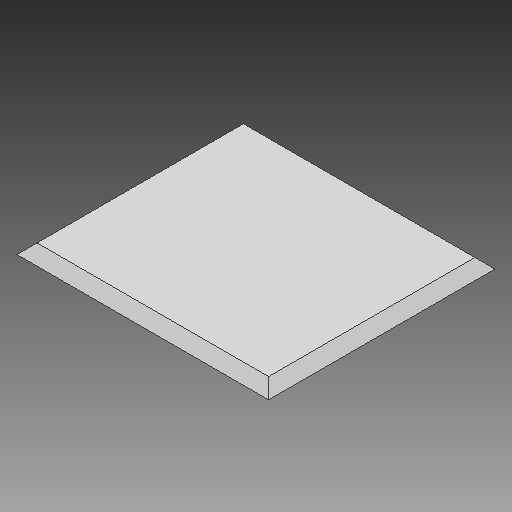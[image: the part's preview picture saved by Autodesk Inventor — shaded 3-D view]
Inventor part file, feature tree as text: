
AUTODESK INVENTOR PART (.ipt)
format: ipt  version: 2018 (Build 220112000, 112)  size: 81,408 bytes
history: native  units: mm
features: other x3, sketch x1
ambient origin geometry x8: Origin, YZ Plane, XZ Plane, XY Plane, X Axis, Y Axis, Z Axis, Center Point
bodies: Volumenkörper1 (feature_tree)
feature tree (4):
  other  "Wand1.ipt"
  other  "Volumenkörper1::Wand1.ipt"
  other  "Bezeichnung1"
  sketch  "Skizze1"  dims[d0=10.0mm]
